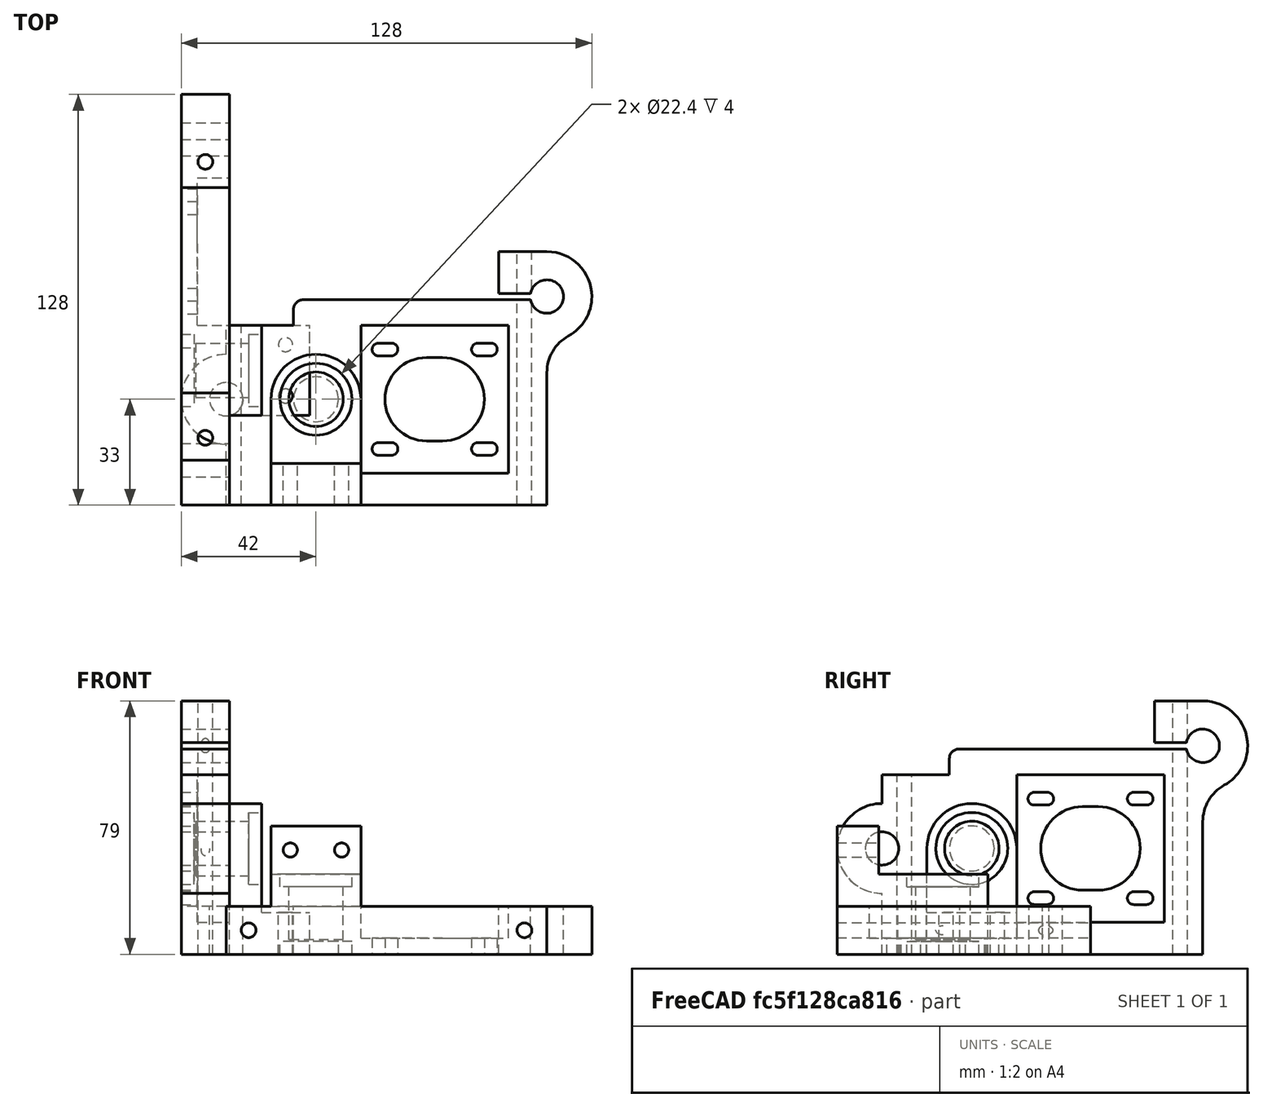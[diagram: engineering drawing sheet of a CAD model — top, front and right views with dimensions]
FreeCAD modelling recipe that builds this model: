
FCSTD DOCUMENT  (FreeCAD 0.15R4527 (Git))
Label: x_motor_holder
License: All rights reserved
LicenseURL: http://en.wikipedia.org/wiki/All_rights_reserved
objects: Part::Cylinder×13, Part::Cut×9, Part::MultiFuse×8, Part::Box×7, Part::Feature×2, Part::Fillet×2, Mesh::Feature×1, Sketcher::SketchObject×1, Part::Extrusion×1
note: 43 computed .brp shape members not serialized (recipe doc carries the construction recipe); baked Part::Feature solids carry a one-line shape summary decoded from their .brp

FEATURE [Mesh::Feature] Xmotorholder
FEATURE [Part::Feature] Xmotorholder001001  label="Xmotorholder002"
  shape: bbox 128 x 79.02 x 40 mm, 2275 faces, 0 solids (baked)
FEATURE [Part::Box] Box  label="Cubo"
  Height = 15
  Length = 100
  Placement = pos=(14,0,0) rot=(0,0,1;0rad)
  Width = 56
FEATURE [Part::Box] Box001  label="Cubo001"
  Height = 15
  Length = 64
  Placement = pos=(35,56,0) rot=(0,0,1;0rad)
  Width = 8
FEATURE [Part::Box] Box002  label="Cubo002"
  Height = 15
  Length = 15
  Placement = pos=(99,56,0) rot=(0,0,1;0rad)
  Width = 23
FEATURE [Part::Cylinder] Cylinder  label="Cilindro"
  Angle = 360
  Height = 15
  Placement = pos=(14,33,0) rot=(0,0,1;0rad)
  Radius = 14
FEATURE [Part::Cylinder] Cylinder001  label="Cilindro001"
  Angle = 360
  Height = 15
  Placement = pos=(114,65,0) rot=(0,0,1;0rad)
  Radius = 14
FEATURE [Part::MultiFuse] Fusion
  Shapes = -> [Box,Cylinder001,Box002,Box001,Cylinder]
FEATURE [Part::Fillet] Fillet
  Base = -> Fusion
  Edges = 1 edges r=13: [Edge15]
FEATURE [Part::Fillet] Fillet001
  Base = -> Fillet
  Edges = 1 edges r=3: [Edge56]
FEATURE [Part::Box] Box003  label="Cubo003"
  Height = 10
  Length = 28
  Placement = pos=(28,0,15) rot=(0,0,1;0rad)
  Width = 33
FEATURE [Part::Cylinder] Cylinder002  label="Cilindro002"
  Angle = 360
  Height = 10
  Placement = pos=(42,33,15) rot=(0,0,1;0rad)
  Radius = 14
FEATURE [Part::MultiFuse] Fusion001
  Shapes = -> [Box003,Cylinder002]
FEATURE [Part::MultiFuse] Fusion002
  Shapes = -> [Fillet001,Fusion001]
FEATURE [Part::Box] Box004  label="Cubo004"
  Height = 15
  Length = 28
  Placement = pos=(28,0,25) rot=(0,0,1;0rad)
  Width = 13
FEATURE [Part::MultiFuse] Fusion003
  Shapes = -> [Fusion002,Box004]
FEATURE [Part::Cylinder] Cylinder003  label="Cilindro003"
  Angle = 360
  Height = 17
  Placement = pos=(14,33,-1) rot=(0,0,1;0rad)
  Radius = 5.2
FEATURE [Part::Cylinder] Cylinder004  label="Cilindro004"
  Angle = 360
  Height = 17
  Placement = pos=(114,65,-1) rot=(0,0,1;0rad)
  Radius = 5.2
FEATURE [Part::MultiFuse] Fusion004
  Shapes = -> [Cylinder003,Cylinder004]
FEATURE [Part::Cut] Cut
  Base = -> Fusion003
  Tool = -> Fusion004
FEATURE [Part::Cylinder] Cylinder005  label="Cilindro005"
  Angle = 360
  Height = 58
  Placement = pos=(21,-1,7.5) rot=(-1,0,0;1.5708rad)
  Radius = 2.3
FEATURE [Part::Cylinder] Cylinder006  label="Cilindro006"
  Angle = 360
  Height = 81
  Placement = pos=(107,-1,7.5) rot=(-1,0,0;1.5708rad)
  Radius = 2.3
FEATURE [Part::MultiFuse] Fusion005
  Shapes = -> [Cylinder005,Cylinder006]
FEATURE [Part::Cut] Cut001
  Base = -> Cut
  Tool = -> Fusion005
FEATURE [Part::Cylinder] Cylinder007  label="Cilindro007"
  Angle = 360
  Height = 15
  Placement = pos=(34,-1,32.5) rot=(-1,0,0;1.5708rad)
  Radius = 2.2
FEATURE [Part::Cylinder] Cylinder008  label="Cilindro008"
  Angle = 360
  Height = 15
  Placement = pos=(50,-1,32.5) rot=(-1,0,0;1.5708rad)
  Radius = 2.2
FEATURE [Part::MultiFuse] Fusion006
  Shapes = -> [Cylinder007,Cylinder008]
FEATURE [Part::Cut] Cut002
  Base = -> Cut001
  Tool = -> Fusion006
FEATURE [Part::Box] Box005  label="Cubo005"
  Height = 10
  Length = 46
  Placement = pos=(56,10,5) rot=(0,0,1;0rad)
  Width = 46
FEATURE [Part::Cut] Cut003
  Base = -> Cut002
  Tool = -> Box005
FEATURE [Part::Cylinder] Cylinder009  label="Cilindro009"
  Angle = 360
  Height = 21
  Placement = pos=(42,33,4.5) rot=(0,0,1;0rad)
  Radius = 8.5
FEATURE [Part::Cut] Cut004
  Base = -> Cut003
  Tool = -> Cylinder009
FEATURE [Part::Cylinder] Cylinder010  label="Cilindro010"
  Angle = 360
  Height = 5
  Placement = pos=(42,33,21) rot=(0,0,1;0rad)
  Radius = 11.2
FEATURE [Part::Cut] Cut005
  Base = -> Cut004
  Tool = -> Cylinder010
FEATURE [Part::Cylinder] Cylinder011  label="Cilindro011"
  Angle = 360
  Height = 5
  Placement = pos=(42,33,-1) rot=(0,0,1;0rad)
  Radius = 11.2
FEATURE [Part::Cut] Cut006
  Base = -> Cut005
  Tool = -> Cylinder011
FEATURE [Part::Cylinder] Cylinder012  label="Cilindro012"
  Angle = 360
  Height = 4
  Placement = pos=(42,33,0) rot=(0,0,1;0rad)
  Radius = 7
FEATURE [Part::MultiFuse] Fusion007
  Shapes = -> [Cut006,Cylinder012]
FEATURE [Sketcher::SketchObject] Sketch
  ExternalGeometry = -> [Xmotorholder001001]
  Support = -> Xmotorholder001001 [Face480]
  sketch-geometry (20):
    g0: ArcOfCircle CenterX=61.5 CenterY=17.5 CenterZ=0 NormalX=0 NormalY=0 NormalZ=1 Radius=2 StartAngle=1.5708 EndAngle=4.71239
    g1: ArcOfCircle CenterX=65.5 CenterY=17.5 CenterZ=0 NormalX=0 NormalY=0 NormalZ=1 Radius=2 StartAngle=4.71239 EndAngle=7.85398
    g2: LineSegment StartX=61.5 StartY=15.5 StartZ=0 EndX=65.5 EndY=15.5 EndZ=0
    g3: LineSegment StartX=61.5 StartY=19.5 StartZ=0 EndX=65.5 EndY=19.5 EndZ=0
    g4: ArcOfCircle CenterX=76.5 CenterY=33 CenterZ=0 NormalX=0 NormalY=0 NormalZ=1 Radius=13 StartAngle=1.5708 EndAngle=4.71239
    g5: ArcOfCircle CenterX=81.5 CenterY=33 CenterZ=0 NormalX=0 NormalY=0 NormalZ=1 Radius=13 StartAngle=4.71239 EndAngle=7.85398
    g6: LineSegment StartX=76.5 StartY=20 StartZ=0 EndX=81.5 EndY=20 EndZ=0
    g7: LineSegment StartX=76.5 StartY=46 StartZ=0 EndX=81.5 EndY=46 EndZ=0
    g8: ArcOfCircle CenterX=61.5 CenterY=48.5 CenterZ=0 NormalX=0 NormalY=0 NormalZ=1 Radius=2 StartAngle=1.5708 EndAngle=4.71239
    g9: ArcOfCircle CenterX=65.5 CenterY=48.5 CenterZ=0 NormalX=0 NormalY=0 NormalZ=1 Radius=2 StartAngle=4.71239 EndAngle=7.85398
    g10: LineSegment StartX=61.5 StartY=46.5 StartZ=0 EndX=65.5 EndY=46.5 EndZ=0
    g11: LineSegment StartX=61.5 StartY=50.5 StartZ=0 EndX=65.5 EndY=50.5 EndZ=0
    g12: ArcOfCircle CenterX=92.5 CenterY=48.5 CenterZ=0 NormalX=0 NormalY=0 NormalZ=1 Radius=2.00001 StartAngle=1.5708 EndAngle=4.71239
    g13: ArcOfCircle CenterX=96.5 CenterY=48.5 CenterZ=0 NormalX=0 NormalY=0 NormalZ=1 Radius=2.00001 StartAngle=4.71239 EndAngle=7.85398
    g14: LineSegment StartX=92.5 StartY=46.5 StartZ=0 EndX=96.5 EndY=46.5 EndZ=0
    g15: LineSegment StartX=92.5 StartY=50.5 StartZ=0 EndX=96.5 EndY=50.5 EndZ=0
    g16: ArcOfCircle CenterX=92.5 CenterY=17.5 CenterZ=0 NormalX=0 NormalY=0 NormalZ=1 Radius=2 StartAngle=1.5708 EndAngle=4.71239
    g17: ArcOfCircle CenterX=96.5 CenterY=17.5 CenterZ=0 NormalX=0 NormalY=0 NormalZ=1 Radius=2 StartAngle=4.71239 EndAngle=7.85398
    g18: LineSegment StartX=92.5 StartY=15.5 StartZ=0 EndX=96.5 EndY=15.5 EndZ=0
    g19: LineSegment StartX=92.5 StartY=19.5 StartZ=0 EndX=96.5 EndY=19.5 EndZ=0
  constraints (45):
    c: Tangent(g0,g3) = 1.5708
    c: Tangent(g0,g2) = -1.5708
    c: Tangent(g2,g1) = -1.5708
    c: Tangent(g3,g1) = 1.5708
    c: Horizontal(g2)
    c: Equal(g0,g1)
    c: Coincident(g1,g-10)
    c: Coincident(g-10,g0)
    c: PointOnObject(g-9,g0)
    c: Tangent(g4,g7) = 1.5708
    c: Tangent(g4,g6) = -1.5708
    c: Tangent(g6,g5) = -1.5708
    c: Tangent(g7,g5) = 1.5708
    c: Horizontal(g6)
    c: Equal(g4,g5)
    c: Coincident(g-15,g5)
    c: Coincident(g-15,g4)
    c: PointOnObject(g-14,g4)
    c: Tangent(g8,g11) = 1.5708
    c: Tangent(g8,g10) = -1.5708
    c: Tangent(g10,g9) = -1.5708
    c: Tangent(g11,g9) = 1.5708
    c: Horizontal(g10)
    c: Equal(g8,g9)
    c: Coincident(g9,g-3)
    c: Coincident(g-3,g8)
    c: PointOnObject(g-4,g8)
    c: Tangent(g12,g15) = 1.5708
    c: Tangent(g12,g14) = -1.5708
    c: Tangent(g14,g13) = -1.5708
    c: Tangent(g15,g13) = 1.5708
    c: Horizontal(g14)
    c: Equal(g12,g13)
    c: Coincident(g12,g-6)
    c: PointOnObject(g-7,g12)
    c: Coincident(g13,g-6)
    c: Tangent(g16,g19) = 1.5708
    c: Tangent(g16,g18) = -1.5708
    c: Tangent(g18,g17) = -1.5708
    c: Tangent(g19,g17) = 1.5708
    c: Horizontal(g18)
    c: Equal(g16,g17)
    c: Coincident(g16,g-13)
    c: Coincident(g-13,g17)
    c: PointOnObject(g-12,g16)
FEATURE [Part::Extrusion] Extrude
  Base = -> Sketch
  Dir = (0,0,7)
  Placement = pos=(0,0,-1) rot=(0,0,1;0rad)
  Solid = true
FEATURE [Part::Cut] Cut007
  Base = -> Fusion007
  Tool = -> Extrude
FEATURE [Part::Box] Box006  label="Cubo006"
  Height = 17
  Length = 12
  Placement = pos=(98,64,-1) rot=(0,0,1;0rad)
  Width = 2
FEATURE [Part::Cut] Cut008  label="x_motor_holder"
  Base = -> Cut007
  Tool = -> Box006
FEATURE [Part::Feature] Cut009  label="x_motor_holder001"
  Placement = pos=(0,0,0) rot=(0.57735,0.57735,0.57735;2.0944rad)
  shape: bbox 40 x 128 x 79 mm, 61 faces (baked)
